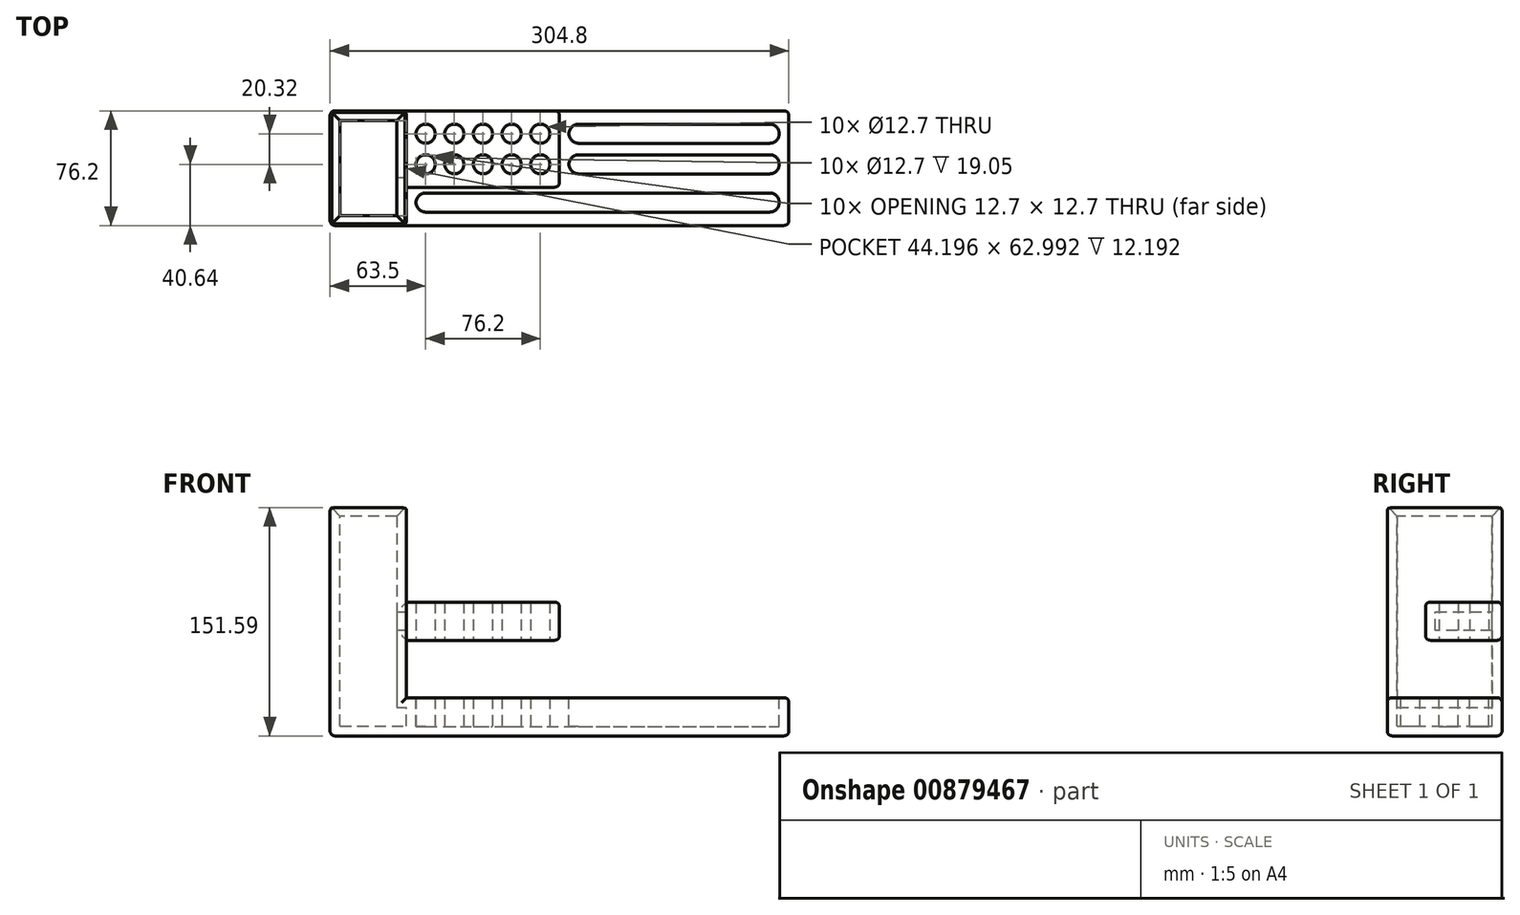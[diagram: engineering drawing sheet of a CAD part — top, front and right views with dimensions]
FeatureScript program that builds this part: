
annotation { "Feature Type Name" : "Feature", "Feature Type Description" : "" }
export const myFeature = defineFeature(function(context is Context, id is Id, definition is map)
    precondition{}
    {
        {
            var Q0;
            Q0=qCreatedBy(makeId("Front.planeOp"),FACE);
            var sketch = newSketch(context, id + "F0", { "sketchPlane" : qUnion([Q0])});
            skLineSegment(sketch, "E0", {"start": v(-152.4, 0) * mm, "end": v(152.4, 0) * mm});
            skLineSegment(sketch, "E1", {"start": v(-152.4, 0) * mm, "end": v(-152.4, 152.4) * mm});
            skLineSegment(sketch, "E2", {"start": v(-152.4, 25.4) * mm, "end": v(152.4, 25.4) * mm});
            skLineSegment(sketch, "E3", {"start": v(152.4, 25.4) * mm, "end": v(152.4, 0) * mm});
            skLineSegment(sketch, "E4", {"start": v(-152.4, 152.4) * mm, "end": v(-101.6, 152.4) * mm});
            skLineSegment(sketch, "E5", {"start": v(-101.6, 152.4) * mm, "end": v(-101.6, 25.4) * mm});
            skLineSegment(sketch, "E6", {"start": v(-101.6, 88.9) * mm, "end": v(0, 88.9) * mm});
            skLineSegment(sketch, "E7", {"start": v(0, 88.9) * mm, "end": v(0, 63.5) * mm});
            skLineSegment(sketch, "E8", {"start": v(0, 63.5) * mm, "end": v(-101.6, 63.5) * mm});
            skSolve(sketch);
        }
        {
            var Q0;
            {var subQ5=sQuery(id+"F0.wireOp",EDGE,"E0");Q0=makeQuery(id+"F0.imprint","IMPRINT",FACE,{"disambiguationData":[TD([[makeQuery(id+"F0.imprint","IMPRINT",EDGE,{"derivedFrom":subQ5}),1.0]])]});}
            var Q1;
            {var subQ0=sQuery(id+"F0.wireOp",EDGE,"E4");Q1=makeQuery(id+"F0.imprint","IMPRINT",FACE,{"disambiguationData":[TD([[makeQuery(id+"F0.imprint","IMPRINT",EDGE,{"derivedFrom":subQ0}),-1.0]])]});}
            extrude(context, id + "F1", {"entities" : qUnion([Q0, Q1]), "depth" : 76.2 * mm, "offsetDistance" : 25.4 * mm});
        }
        {
            var Q0;
            {var subQ0=sQuery(id+"F0.wireOp",EDGE,"E6");Q0=makeQuery(id+"F0.imprint","IMPRINT",FACE,{"disambiguationData":[TD([[makeQuery(id+"F0.imprint","IMPRINT",EDGE,{"derivedFrom":subQ0}),-1.0]])]});}
            extrude(context, id + "F2", {"entities" : qUnion([Q0]), "operationType" : NewBodyOperationType.ADD, "depth" : 50.8 * mm, "offsetDistance" : 25.4 * mm});
        }
        {
            var Q0;
            Q0=makeQuery(id+"F1.opExtrude","SWEPT_FACE",FACE,{"disambiguationData":[OSD([sQuery(id+"F0.wireOp",EDGE,"E4")])]});
            shell(context, id + "F3", {"entities" : qUnion([Q0]), "thickness" : 6.6 * mm});
        }
        {
            var Q0;
            Q0=makeQuery(id+"F1.opExtrude","CAP_EDGE",EDGE,{"disambiguationData":[OSD([sQuery(id+"F0.wireOp",EDGE,"E1")])],"isStart":false});
            var Q1;
            Q1=makeQuery(id+"F1.opExtrude","CAP_EDGE",EDGE,{"disambiguationData":[OSD([sQuery(id+"F0.wireOp",EDGE,"E5")])],"isStart":false});
            var Q2;
            Q2=makeQuery(id+"F2.opExtrude","CAP_EDGE",EDGE,{"disambiguationData":[OSD([sQuery(id+"F0.wireOp",EDGE,"E7")])],"isStart":false});
            var Q3;
            Q3=makeQuery(id+"F2.opExtrude","CAP_EDGE",EDGE,{"disambiguationData":[OSD([sQuery(id+"F0.wireOp",EDGE,"E7")])],"isStart":true});
            var Q4;
            Q4=makeQuery(id+"F1.opExtrude","CAP_EDGE",EDGE,{"disambiguationData":[OSD([sQuery(id+"F0.wireOp",EDGE,"E1")])],"isStart":true});
            var Q5;
            {var subQ1=sQuery(id+"F0.wireOp",EDGE,"E5");var subQ2=sQuery(id+"F0.wireOp",EDGE,"E2");Q5=makeQuery(id+"F2.boolean.opBoolean","SPLIT",EDGE,{"disambiguationData":[TD([makeQuery(id+"F1.opExtrude","SWEPT_FACE",FACE,{"disambiguationData":[OSD([subQ2])]})])],"derivedFrom":makeQuery(id+"F1.opExtrude","CAP_EDGE",EDGE,{"disambiguationData":[OSD([subQ1])],"isStart":true})});}
            var Q6;
            {var subQ1=sQuery(id+"F0.wireOp",EDGE,"E5");var subQ2=sQuery(id+"F0.wireOp",EDGE,"E4");Q6=makeQuery(id+"F2.boolean.opBoolean","SPLIT",EDGE,{"disambiguationData":[TD([makeQuery(id+"F1.opExtrude","SWEPT_FACE",FACE,{"disambiguationData":[OSD([subQ2])]})])],"derivedFrom":makeQuery(id+"F1.opExtrude","CAP_EDGE",EDGE,{"disambiguationData":[OSD([subQ1])],"isStart":true})});}
            var Q7;
            Q7=makeQuery(id+"F1.opExtrude","CAP_EDGE",EDGE,{"disambiguationData":[OSD([sQuery(id+"F0.wireOp",EDGE,"E3")])],"isStart":true});
            var Q8;
            Q8=makeQuery(id+"F1.opExtrude","CAP_EDGE",EDGE,{"disambiguationData":[OSD([sQuery(id+"F0.wireOp",EDGE,"E3")])],"isStart":false});
            var Q9;
            Q9=makeQuery(id+"F2.opExtrude","CAP_EDGE",EDGE,{"disambiguationData":[OSD([sQuery(id+"F0.wireOp",EDGE,"E5")])],"isStart":false});
            var Q10;
            Q10=makeQuery(id+"F2.opExtrude","CAP_EDGE",EDGE,{"disambiguationData":[OSD([sQuery(id+"F0.wireOp",EDGE,"E6")])],"isStart":true});
            var Q11;
            Q11=makeQuery(id+"F2.opExtrude","CAP_EDGE",EDGE,{"disambiguationData":[OSD([sQuery(id+"F0.wireOp",EDGE,"E6")])],"isStart":false});
            var Q12;
            Q12=makeQuery(id+"F2.opExtrude","CAP_EDGE",EDGE,{"disambiguationData":[OSD([sQuery(id+"F0.wireOp",EDGE,"E8")])],"isStart":false});
            var Q13;
            Q13=makeQuery(id+"F2.opExtrude","CAP_EDGE",EDGE,{"disambiguationData":[OSD([sQuery(id+"F0.wireOp",EDGE,"E8")])],"isStart":true});
            var Q14;
            Q14=makeQuery(id+"F1.opExtrude","CAP_EDGE",EDGE,{"disambiguationData":[OSD([sQuery(id+"F0.wireOp",EDGE,"E2")])],"isStart":true});
            var Q15;
            Q15=makeQuery(id+"F1.opExtrude","CAP_EDGE",EDGE,{"disambiguationData":[OSD([sQuery(id+"F0.wireOp",EDGE,"E0")])],"isStart":false});
            var Q16;
            Q16=makeQuery(id+"F1.opExtrude","CAP_EDGE",EDGE,{"disambiguationData":[OSD([sQuery(id+"F0.wireOp",EDGE,"E2")])],"isStart":false});
            var Q17;
            Q17=makeQuery(id+"F1.opExtrude","SWEPT_EDGE",EDGE,{"disambiguationData":[OSD([sQuery(id+"F0.wireOp",EDGE,"E2"),sQuery(id+"F0.wireOp",EDGE,"E3")])]});
            var Q18;
            Q18=makeQuery(id+"F1.opExtrude","SWEPT_EDGE",EDGE,{"disambiguationData":[OSD([sQuery(id+"F0.wireOp",EDGE,"E0"),sQuery(id+"F0.wireOp",EDGE,"E3")])]});
            var Q19;
            Q19=makeQuery(id+"F1.opExtrude","CAP_EDGE",EDGE,{"disambiguationData":[OSD([sQuery(id+"F0.wireOp",EDGE,"E0")])],"isStart":true});
            var Q20;
            Q20=makeQuery(id+"F1.opExtrude","SWEPT_EDGE",EDGE,{"disambiguationData":[OSD([sQuery(id+"F0.wireOp",EDGE,"E0"),sQuery(id+"F0.wireOp",EDGE,"E1")])]});
            var Q21;
            Q21=makeQuery(id+"F2.opExtrude","SWEPT_EDGE",EDGE,{"disambiguationData":[OSD([sQuery(id+"F0.wireOp",EDGE,"E7"),sQuery(id+"F0.wireOp",EDGE,"E8")])]});
            var Q22;
            Q22=makeQuery(id+"F2.opExtrude","SWEPT_EDGE",EDGE,{"disambiguationData":[OSD([sQuery(id+"F0.wireOp",EDGE,"E6"),sQuery(id+"F0.wireOp",EDGE,"E7")])]});
            var Q23;
            Q23=makeQuery(id+"F1.opExtrude","SWEPT_EDGE",EDGE,{"disambiguationData":[OSD([sQuery(id+"F0.wireOp",EDGE,"E4"),sQuery(id+"F0.wireOp",EDGE,"E5")])]});
            var Q24;
            Q24=makeQuery(id+"F1.opExtrude","SWEPT_EDGE",EDGE,{"disambiguationData":[OSD([sQuery(id+"F0.wireOp",EDGE,"E1"),sQuery(id+"F0.wireOp",EDGE,"E4")])]});
            var Q25;
            Q25=makeQuery(id+"F1.opExtrude","CAP_EDGE",EDGE,{"disambiguationData":[OSD([sQuery(id+"F0.wireOp",EDGE,"E4")])],"isStart":false});
            var Q26;
            Q26=makeQuery(id+"F1.opExtrude","CAP_EDGE",EDGE,{"disambiguationData":[OSD([sQuery(id+"F0.wireOp",EDGE,"E4")])],"isStart":true});
            fillet(context, id + "F4", {"entities" : qUnion([Q0, Q1, Q2, Q3, Q4, Q5, Q6, Q7, Q8, Q9, Q10, Q11, Q12, Q13, Q14, Q15, Q16, Q17, Q18, Q19, Q20, Q21, Q22, Q23, Q24, Q25, Q26]), "radius" : 3.17 * mm, "tangentPropagation" : true, "allowEdgeOverflow" : false});
        }
        {
            var Q0;
            Q0=qCreatedBy(makeId("Top.planeOp"),FACE);
            var sketch = newSketch(context, id + "F5", { "sketchPlane" : qUnion([Q0])});
            skCircle(sketch, "E9", {"center": v(-12.7, -35.56) * mm, "radius": 6.35 * mm});
            skCircle(sketch, "E10.0.1.0", {"center": v(-12.7, -15.24) * mm, "radius": 6.35 * mm});
            skCircle(sketch, "E10.1.0.0", {"center": v(-31.75, -35.56) * mm, "radius": 6.35 * mm});
            skCircle(sketch, "E10.1.1.0", {"center": v(-31.75, -15.24) * mm, "radius": 6.35 * mm});
            skCircle(sketch, "E10.2.0.0", {"center": v(-50.8, -35.56) * mm, "radius": 6.35 * mm});
            skCircle(sketch, "E10.2.1.0", {"center": v(-50.8, -15.24) * mm, "radius": 6.35 * mm});
            skCircle(sketch, "E10.3.0.0", {"center": v(-69.85, -35.56) * mm, "radius": 6.35 * mm});
            skCircle(sketch, "E10.3.1.0", {"center": v(-69.85, -15.24) * mm, "radius": 6.35 * mm});
            skCircle(sketch, "E10.4.0.0", {"center": v(-88.9, -35.56) * mm, "radius": 6.35 * mm});
            skCircle(sketch, "E10.4.1.0", {"center": v(-88.9, -15.24) * mm, "radius": 6.35 * mm});
            skLineSegment(sketch, "E10.direction1", {"start": v(-12.7, -35.56) * mm, "end": v(-31.75, -35.56) * mm, "construction": true});
            skLineSegment(sketch, "E10.direction2", {"start": v(-12.7, -35.56) * mm, "end": v(-12.7, -15.24) * mm, "construction": true});
            skSolve(sketch);
        }
        {
            var Q0;
            Q0 = qSketchRegion(id + "F5", true);
            extrude(context, id + "F6", {"entities" : qUnion([Q0]), "operationType" : NewBodyOperationType.REMOVE, "depth" : 95.25 * mm, "offsetDistance" : 25.4 * mm});
        }
        {
            var Q0;
            Q0=makeQuery(id+"F1.opExtrude","SWEPT_FACE",FACE,{"disambiguationData":[OSD([sQuery(id+"F0.wireOp",EDGE,"E0")])]});
            var sketch = newSketch(context, id + "F7", { "sketchPlane" : qUnion([Q0])});
            skLineSegment(sketch, "E11.bottom", {"start": v(-108.5, 48.75) * mm, "end": v(10.99, 48.75) * mm});
            skLineSegment(sketch, "E11.top", {"start": v(-108.5, 5.44) * mm, "end": v(10.99, 5.44) * mm});
            skLineSegment(sketch, "E11.left", {"start": v(-108.5, 48.75) * mm, "end": v(-108.5, 5.44) * mm});
            skLineSegment(sketch, "E11.right", {"start": v(10.99, 48.75) * mm, "end": v(10.99, 5.44) * mm});
            skSolve(sketch);
        }
        {
            var Q0;
            Q0 = qSketchRegion(id + "F7", true);
            extrude(context, id + "F8", {"entities" : qUnion([Q0]), "operationType" : NewBodyOperationType.ADD, "oppositeDirection" : true, "depth" : 6.35 * mm, "offsetDistance" : 25.4 * mm});
        }
        {
            var Q0;
            Q0=makeQuery(id+"F1.opExtrude","SWEPT_FACE",FACE,{"disambiguationData":[OSD([sQuery(id+"F0.wireOp",EDGE,"E2")])]});
            var sketch = newSketch(context, id + "F9", { "sketchPlane" : qUnion([Q0])});
            skCircle(sketch, "E12", {"center": v(12.7, -15.24) * mm, "radius": 6.35 * mm});
            skCircle(sketch, "E13", {"center": v(139.7, -15.24) * mm, "radius": 6.35 * mm});
            skLineSegment(sketch, "E14", {"start": v(12.7, -21.59) * mm, "end": v(139.7, -21.59) * mm});
            skLineSegment(sketch, "E15", {"start": v(12.7, -8.89) * mm, "end": v(139.7, -8.89) * mm});
            skCircle(sketch, "E16.0.1.0", {"center": v(12.7, -35.56) * mm, "radius": 6.35 * mm});
            skLineSegment(sketch, "E16.0.1.1", {"start": v(12.7, -41.91) * mm, "end": v(139.7, -41.91) * mm});
            skLineSegment(sketch, "E16.0.1.2", {"start": v(12.7, -29.21) * mm, "end": v(139.7, -29.2) * mm});
            skCircle(sketch, "E16.0.1.3", {"center": v(139.7, -35.56) * mm, "radius": 6.35 * mm});
            skLineSegment(sketch, "E16.direction1", {"start": v(12.7, -15.24) * mm, "end": v(38.1, -15.24) * mm, "construction": true});
            skLineSegment(sketch, "E16.direction2", {"start": v(12.7, -15.24) * mm, "end": v(12.7, -35.56) * mm, "construction": true});
            skCircle(sketch, "E17", {"center": v(-88.9, -60.96) * mm, "radius": 6.35 * mm});
            skCircle(sketch, "E18", {"center": v(139.7, -60.96) * mm, "radius": 6.35 * mm});
            skLineSegment(sketch, "E19", {"start": v(139.7, -15.24) * mm, "end": v(139.7, -86.82) * mm, "construction": true});
            skLineSegment(sketch, "E20", {"start": v(-88.9, -67.3) * mm, "end": v(139.7, -67.3) * mm});
            skLineSegment(sketch, "E21", {"start": v(-88.9, -54.6) * mm, "end": v(139.7, -54.6) * mm});
            skSolve(sketch);
        }
        {
            var Q0;
            {var subQ0=sQuery(id+"F9.wireOp",EDGE,"E20");Q0=makeQuery(id+"F9.imprint","IMPRINT",FACE,{"disambiguationData":[TD([[makeQuery(id+"F9.imprint","IMPRINT",EDGE,{"derivedFrom":subQ0}),1.0]])]});}
            var Q1;
            {var subQ0=sQuery(id+"F9.wireOp",EDGE,"E16.0.1.1");Q1=makeQuery(id+"F9.imprint","IMPRINT",FACE,{"disambiguationData":[TD([[makeQuery(id+"F9.imprint","IMPRINT",EDGE,{"derivedFrom":subQ0}),1.0]])]});}
            var Q2;
            {var subQ0=sQuery(id+"F9.wireOp",EDGE,"E14");Q2=makeQuery(id+"F9.imprint","IMPRINT",FACE,{"disambiguationData":[TD([[makeQuery(id+"F9.imprint","IMPRINT",EDGE,{"derivedFrom":subQ0}),1.0]])]});}
            var Q3;
            {var subQ0=sQuery(id+"F9.wireOp",EDGE,"E18");var subQ1=makeQuery(id+"F9.imprint","INTERSECT",VERTEX,{"derivedFrom":[subQ0,sQuery(id+"F9.wireOp",EDGE,"E20")]});Q3=makeQuery(id+"F9.imprint","IMPRINT",FACE,{"disambiguationData":[TD([[makeQuery(id+"F9.imprint","IMPRINT",EDGE,{"disambiguationData":[TD([[subQ1,1.0]])],"derivedFrom":subQ0}),1.0]])]});}
            var Q4;
            {var subQ0=sQuery(id+"F9.wireOp",EDGE,"E13");var subQ1=makeQuery(id+"F9.imprint","INTERSECT",VERTEX,{"derivedFrom":[subQ0,sQuery(id+"F9.wireOp",EDGE,"E14")]});Q4=makeQuery(id+"F9.imprint","IMPRINT",FACE,{"disambiguationData":[TD([[makeQuery(id+"F9.imprint","IMPRINT",EDGE,{"disambiguationData":[TD([[subQ1,1.0]])],"derivedFrom":subQ0}),1.0]])]});}
            var Q5;
            {var subQ0=sQuery(id+"F9.wireOp",EDGE,"E16.0.1.3");var subQ1=makeQuery(id+"F9.imprint","INTERSECT",VERTEX,{"derivedFrom":[sQuery(id+"F9.wireOp",EDGE,"E16.0.1.1"),subQ0]});Q5=makeQuery(id+"F9.imprint","IMPRINT",FACE,{"disambiguationData":[TD([[makeQuery(id+"F9.imprint","IMPRINT",EDGE,{"disambiguationData":[TD([[subQ1,1.0]])],"derivedFrom":subQ0}),1.0]])]});}
            var Q6;
            {var subQ0=sQuery(id+"F9.wireOp",EDGE,"E16.0.1.0");var subQ1=makeQuery(id+"F9.imprint","INTERSECT",VERTEX,{"derivedFrom":[subQ0,sQuery(id+"F9.wireOp",EDGE,"E16.0.1.1")]});Q6=makeQuery(id+"F9.imprint","IMPRINT",FACE,{"disambiguationData":[TD([[makeQuery(id+"F9.imprint","IMPRINT",EDGE,{"disambiguationData":[TD([[subQ1,1.0]])],"derivedFrom":subQ0}),1.0]])]});}
            var Q7;
            {var subQ0=sQuery(id+"F9.wireOp",EDGE,"E12");var subQ1=makeQuery(id+"F9.imprint","INTERSECT",VERTEX,{"derivedFrom":[subQ0,sQuery(id+"F9.wireOp",EDGE,"E14")]});Q7=makeQuery(id+"F9.imprint","IMPRINT",FACE,{"disambiguationData":[TD([[makeQuery(id+"F9.imprint","IMPRINT",EDGE,{"disambiguationData":[TD([[subQ1,1.0]])],"derivedFrom":subQ0}),1.0]])]});}
            var Q8;
            {var subQ0=sQuery(id+"F9.wireOp",EDGE,"E17");var subQ1=makeQuery(id+"F9.imprint","INTERSECT",VERTEX,{"derivedFrom":[subQ0,sQuery(id+"F9.wireOp",EDGE,"E20")]});Q8=makeQuery(id+"F9.imprint","IMPRINT",FACE,{"disambiguationData":[TD([[makeQuery(id+"F9.imprint","IMPRINT",EDGE,{"disambiguationData":[TD([[subQ1,1.0]])],"derivedFrom":subQ0}),1.0]])]});}
            extrude(context, id + "F10", {"entities" : qUnion([Q0, Q1, Q2, Q3, Q4, Q5, Q6, Q7, Q8]), "operationType" : NewBodyOperationType.REMOVE, "oppositeDirection" : true, "depth" : 19.05 * mm, "offsetDistance" : 25.4 * mm});
        }
        {
            var Q0;
            Q0=makeQuery(id+"F2.opExtrude","SWEPT_FACE",FACE,{"disambiguationData":[OSD([sQuery(id+"F0.wireOp",EDGE,"E6")])]});
            extrude(context, id + "F11", {"entities" : qUnion([Q0]), "operationType" : NewBodyOperationType.ADD, "oppositeDirection" : true, "depth" : 25.4 * mm, "offsetDistance" : 25.4 * mm});
        }
        {
            var Q0;
            Q0=makeQuery(id+"F1.opExtrude","SWEPT_FACE",FACE,{"disambiguationData":[OSD([sQuery(id+"F0.wireOp",EDGE,"E2")])]});
            extrude(context, id + "F12", {"entities" : qUnion([Q0]), "operationType" : NewBodyOperationType.ADD, "oppositeDirection" : true, "depth" : 25.4 * mm, "offsetDistance" : 25.4 * mm});
        }
        {
            var Q0;
            Q0=makeQuery(id+"F1.opExtrude","SWEPT_FACE",FACE,{"disambiguationData":[OSD([sQuery(id+"F0.wireOp",EDGE,"E4")])]});
            var Q1;
            {var subQ0=sQuery(id+"F0.wireOp",EDGE,"E4");var subQ1=sQuery(id+"F0.wireOp",EDGE,"E1");Q1=makeQuery(id+"F4.opFillet","BLEND_FACE",FACE,{"disambiguationData":[OSD([subQ1,subQ0]),TDD([makeQuery(id+"F1.opExtrude","SWEPT_EDGE",EDGE,{"disambiguationData":[OSD([subQ1,subQ0])]})])]});}
            var Q2;
            {var subQ0=sQuery(id+"F0.wireOp",EDGE,"E4");Q2=makeQuery(id+"F4.opFillet","BLEND_FACE",FACE,{"disambiguationData":[OSD([subQ0]),TDD([makeQuery(id+"F1.opExtrude","CAP_EDGE",EDGE,{"disambiguationData":[OSD([subQ0])],"isStart":false})])]});}
            var Q3;
            {var subQ0=sQuery(id+"F0.wireOp",EDGE,"E4");var subQ1=sQuery(id+"F0.wireOp",EDGE,"E1");Q3=makeQuery(id+"F4.opFillet","BLEND_FACE",FACE,{"disambiguationData":[OSD([subQ1,subQ0]),TDD([makeQuery(id+"F1.opExtrude","CAP_VERTEX",VERTEX,{"disambiguationData":[OSD([subQ1,subQ0])],"isStart":false})])]});}
            var Q4;
            {var subQ0=sQuery(id+"F0.wireOp",EDGE,"E5");var subQ1=sQuery(id+"F0.wireOp",EDGE,"E4");Q4=makeQuery(id+"F4.opFillet","BLEND_FACE",FACE,{"disambiguationData":[OSD([subQ1,subQ0]),TDD([makeQuery(id+"F1.opExtrude","CAP_VERTEX",VERTEX,{"disambiguationData":[OSD([subQ1,subQ0])],"isStart":false})])]});}
            var Q5;
            {var subQ0=sQuery(id+"F0.wireOp",EDGE,"E5");var subQ1=sQuery(id+"F0.wireOp",EDGE,"E4");Q5=makeQuery(id+"F4.opFillet","BLEND_FACE",FACE,{"disambiguationData":[OSD([subQ1,subQ0]),TDD([makeQuery(id+"F1.opExtrude","SWEPT_EDGE",EDGE,{"disambiguationData":[OSD([subQ1,subQ0])]})])]});}
            var Q6;
            {var subQ0=sQuery(id+"F0.wireOp",EDGE,"E4");Q6=makeQuery(id+"F4.opFillet","BLEND_FACE",FACE,{"disambiguationData":[OSD([subQ0]),TDD([makeQuery(id+"F1.opExtrude","CAP_EDGE",EDGE,{"disambiguationData":[OSD([subQ0])],"isStart":true})])]});}
            var Q7;
            {var subQ0=sQuery(id+"F0.wireOp",EDGE,"E5");var subQ1=sQuery(id+"F0.wireOp",EDGE,"E4");Q7=makeQuery(id+"F4.opFillet","BLEND_FACE",FACE,{"disambiguationData":[OSD([subQ1,subQ0]),TDD([makeQuery(id+"F1.opExtrude","CAP_VERTEX",VERTEX,{"disambiguationData":[OSD([subQ1,subQ0])],"isStart":true})])]});}
            var Q8;
            {var subQ0=sQuery(id+"F0.wireOp",EDGE,"E4");var subQ1=sQuery(id+"F0.wireOp",EDGE,"E1");Q8=makeQuery(id+"F4.opFillet","BLEND_FACE",FACE,{"disambiguationData":[OSD([subQ1,subQ0]),TDD([makeQuery(id+"F1.opExtrude","CAP_VERTEX",VERTEX,{"disambiguationData":[OSD([subQ1,subQ0])],"isStart":true})])]});}
            chamfer(context, id + "F13", {"entities" : qUnion([Q0, Q1, Q2, Q3, Q4, Q5, Q6, Q7, Q8]), "width" : 6.35 * mm, "tangentPropagation" : true});
        }
    });
